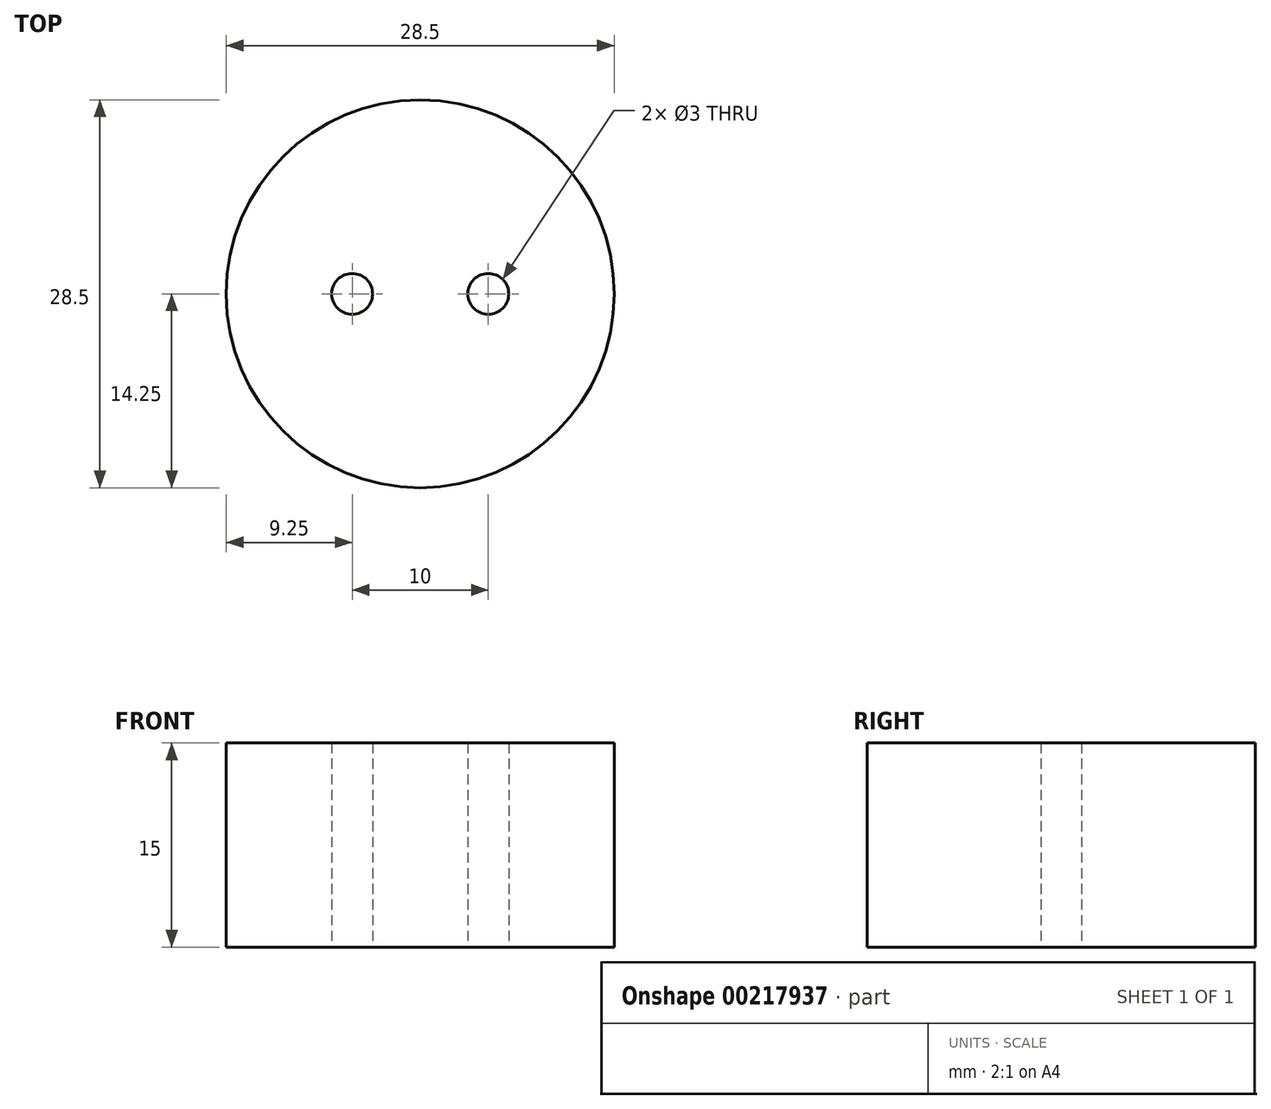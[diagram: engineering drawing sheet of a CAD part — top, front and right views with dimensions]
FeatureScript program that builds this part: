
annotation { "Feature Type Name" : "Feature", "Feature Type Description" : "" }
export const myFeature = defineFeature(function(context is Context, id is Id, definition is map)
    precondition{}
    {
        {
            var Q0;
            Q0=qCreatedBy(makeId("Top.planeOp"),FACE);
            var sketch = newSketch(context, id + "F0", { "sketchPlane" : qUnion([Q0])});
            skCircle(sketch, "E0", {"center": v(0, 0) * mm, "radius": 14.25 * mm});
            skLineSegment(sketch, "E1", {"start": v(0, 0) * mm, "end": v(5, 0) * mm});
            skLineSegment(sketch, "E2", {"start": v(0, 0) * mm, "end": v(-5, 0) * mm});
            skCircle(sketch, "E3", {"center": v(-5, 0) * mm, "radius": 1.5 * mm});
            skCircle(sketch, "E4", {"center": v(5, 0) * mm, "radius": 1.5 * mm});
            skSolve(sketch);
        }
        {
            var Q0;
            Q0=makeQuery(id+"F0.imprint","IMPRINT",FACE,{"disambiguationData":[TD([[makeQuery(id+"F0.imprint","IMPRINT",EDGE,{"derivedFrom":sQuery(id+"F0.wireOp",EDGE,"E0")}),1.0]])]});
            extrude(context, id + "F1", {"entities" : qUnion([Q0]), "depth" : 15 * mm});
        }
    });
